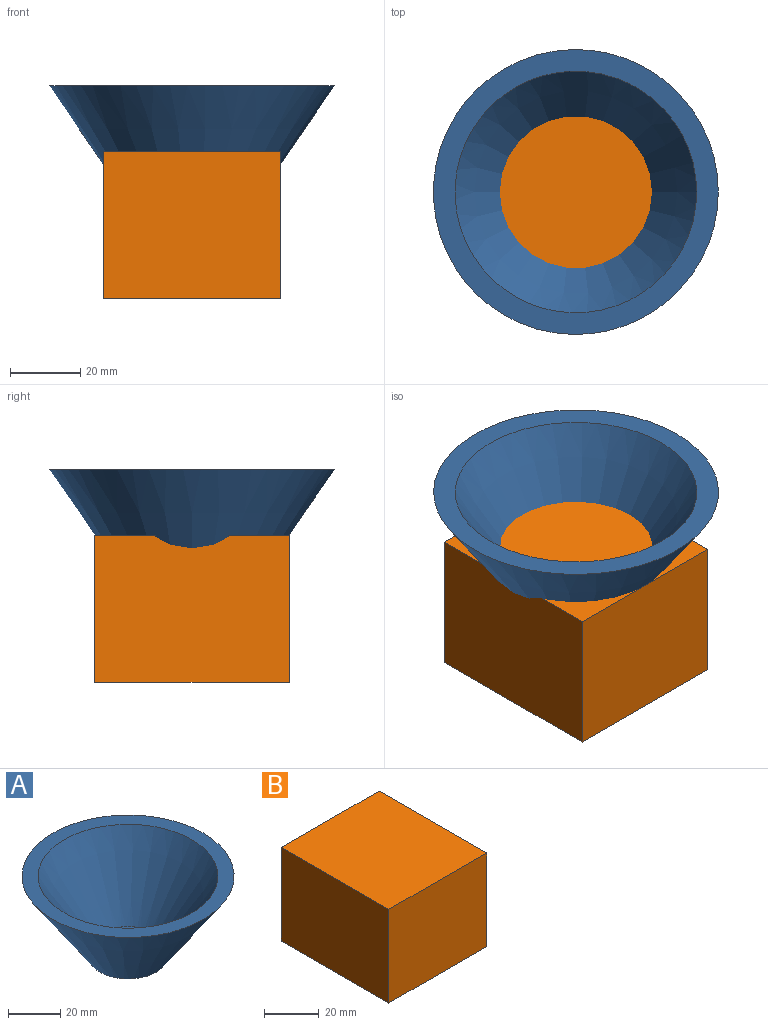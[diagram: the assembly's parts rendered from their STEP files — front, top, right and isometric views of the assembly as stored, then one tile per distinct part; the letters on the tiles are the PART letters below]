
ASSEMBLY  parts=2 mates=1
PART A: 5 faces, bbox 80.9x80.9x37.3 mm
  f0: plane 24.77x24.77mm, normal (0,0,1), area 481.7mm2, adj f4
  f1: plane 30.14x30.14mm, normal (0,0,-1), area 713.5mm2, adj f2
  f2: cone r=15.07mm half-angle=34.3deg, axis (0,0,1), area 7874.3mm2, adj f1,f3
  f3: plane 80.94x80.94mm, normal (0,0,1), area 1444.1mm2, adj f2,f4
  f4: cone r=12.38mm half-angle=34.3deg, axis (0,0,1), area 5720.2mm2, adj f0,f3
PART B: 6 faces, bbox 50.4x55.4x41.8 mm
  f0: plane 55.4x41.84mm, normal (-1,0,0), area 2317.9mm2, adj f1,f3,f4,f5
  f1: plane 55.4x50.4mm, normal (0,0,-1), area 2792.4mm2, adj f0,f2,f4,f5
  f2: plane 55.4x41.84mm, normal (1,0,0), area 2317.9mm2, adj f1,f3,f4,f5
  f3: plane 55.4x50.4mm, normal (0,0,1), area 2792.4mm2, adj f0,f2,f4,f5
  f4: plane 50.4x41.84mm, normal (0,-1,0), area 2108.9mm2, adj f0,f1,f2,f3
  f5: plane 50.4x41.84mm, normal (0,1,0), area 2108.9mm2, adj f0,f1,f2,f3
PLACE A at identity fixed
PLACE B t=(-4.89,-2.3,-23.38)mm
MATE fastened B.f3 <-> A.f2  axis (0,0,1) through (0,0,-0.38)mm
